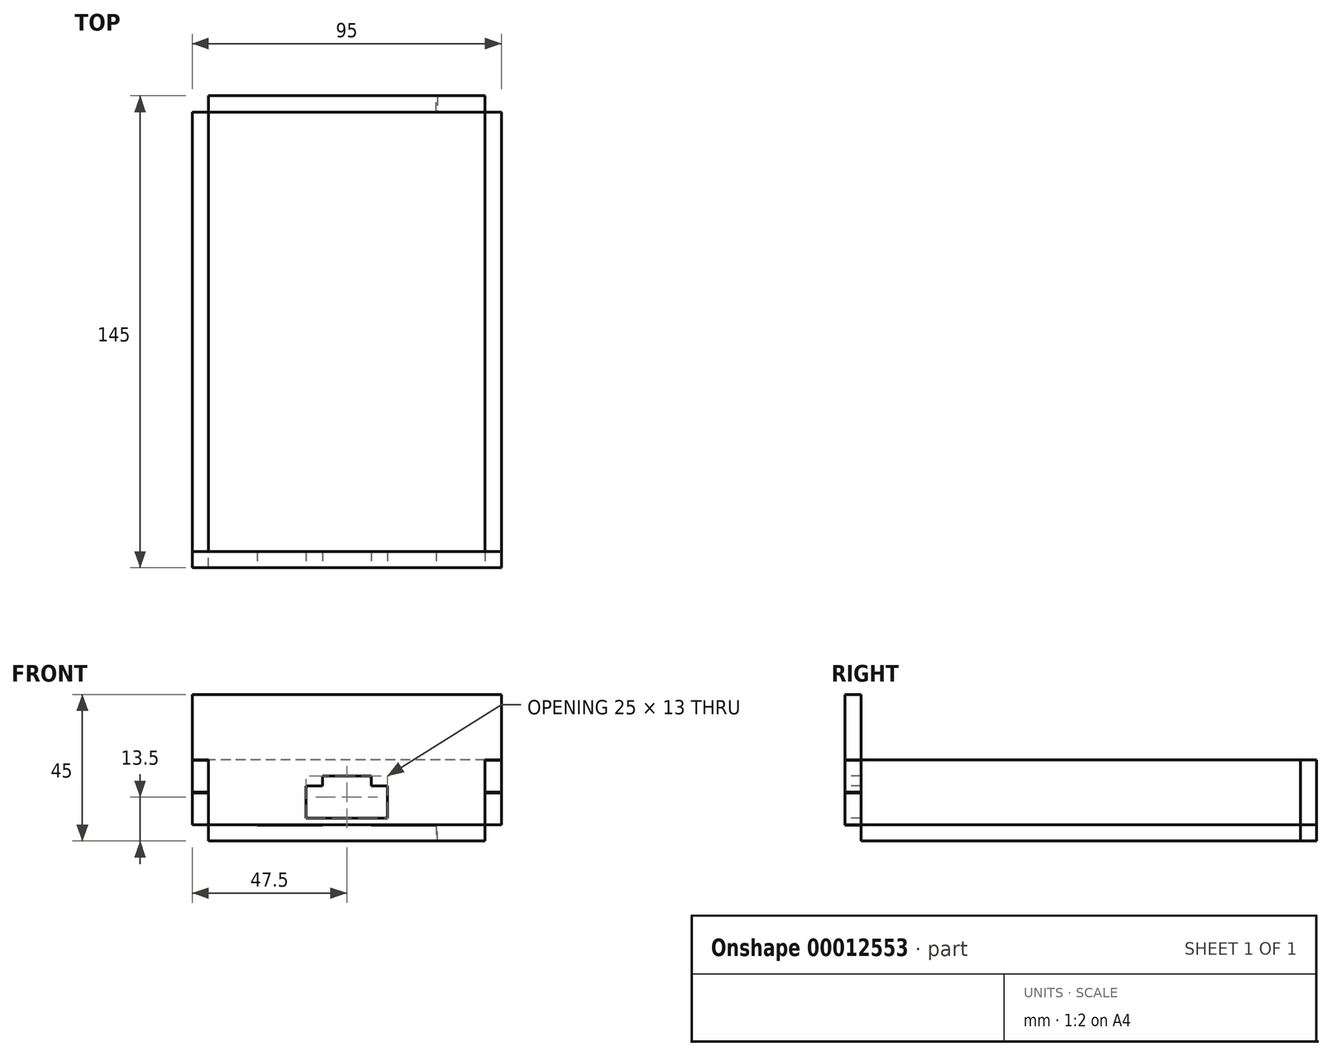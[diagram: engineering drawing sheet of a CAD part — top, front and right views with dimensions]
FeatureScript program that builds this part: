
annotation { "Feature Type Name" : "Feature", "Feature Type Description" : "" }
export const myFeature = defineFeature(function(context is Context, id is Id, definition is map)
    precondition{}
    {
        {
            var Q0;
            Q0=qCreatedBy(makeId("Top.planeOp"),FACE);
            var sketch = newSketch(context, id + "F0", { "sketchPlane" : qUnion([Q0])});
            skLineSegment(sketch, "E0.bottom", {"start": v(0, 0) * mm, "end": v(-95, 0) * mm});
            skLineSegment(sketch, "E0.top", {"start": v(0, 145) * mm, "end": v(-95, 145) * mm});
            skLineSegment(sketch, "E0.left", {"start": v(0, 0) * mm, "end": v(0, 145) * mm});
            skLineSegment(sketch, "E0.right", {"start": v(-95, 0) * mm, "end": v(-95, 145) * mm});
            skSolve(sketch);
        }
        {
            var Q0;
            Q0 = qSketchRegion(id + "F0", true);
            extrude(context, id + "F1", {"entities" : qUnion([Q0]), "depth" : 5 * mm});
        }
        {
            var Q0;
            Q0=makeQuery(id+"F1.opExtrude","SWEPT_FACE",FACE,{"disambiguationData":[OSD([sQuery(id+"F0.wireOp",EDGE,"E0.bottom")])]});
            var sketch = newSketch(context, id + "F2", { "sketchPlane" : qUnion([Q0])});
            skLineSegment(sketch, "E1.bottom", {"start": v(0, 0) * mm, "end": v(-95, 0) * mm});
            skLineSegment(sketch, "E1.top", {"start": v(0, 45) * mm, "end": v(-95, 45) * mm});
            skLineSegment(sketch, "E1.left", {"start": v(0, 0) * mm, "end": v(0, 45) * mm});
            skLineSegment(sketch, "E1.right", {"start": v(-95, 0) * mm, "end": v(-95, 45) * mm});
            skSolve(sketch);
        }
        {
            var Q0;
            Q0 = qSketchRegion(id + "F2", true);
            extrude(context, id + "F3", {"entities" : qUnion([Q0]), "oppositeDirection" : true, "depth" : 5 * mm});
        }
        {
            var Q0;
            Q0=makeQuery(id+"F1.opExtrude","SWEPT_FACE",FACE,{"disambiguationData":[OSD([sQuery(id+"F0.wireOp",EDGE,"E0.left")])]});
            var sketch = newSketch(context, id + "F4", { "sketchPlane" : qUnion([Q0])});
            skLineSegment(sketch, "E2.bottom", {"start": v(0, 0) * mm, "end": v(145, 0) * mm});
            skLineSegment(sketch, "E2.top", {"start": v(0, 25) * mm, "end": v(145, 25) * mm});
            skLineSegment(sketch, "E2.left", {"start": v(0, 0) * mm, "end": v(0, 25) * mm});
            skLineSegment(sketch, "E2.right", {"start": v(145, 0) * mm, "end": v(145, 25) * mm});
            skSolve(sketch);
        }
        {
            var Q0;
            Q0 = qSketchRegion(id + "F4", true);
            extrude(context, id + "F5", {"entities" : qUnion([Q0]), "oppositeDirection" : true, "depth" : 5 * mm});
        }
        {
            var Q0;
            Q0=makeQuery(id+"F1.opExtrude","SWEPT_FACE",FACE,{"disambiguationData":[OSD([sQuery(id+"F0.wireOp",EDGE,"E0.right")])]});
            var sketch = newSketch(context, id + "F6", { "sketchPlane" : qUnion([Q0])});
            skLineSegment(sketch, "E3.bottom", {"start": v(-145, 0) * mm, "end": v(0, 0) * mm});
            skLineSegment(sketch, "E3.top", {"start": v(-145, 25) * mm, "end": v(0, 25) * mm});
            skLineSegment(sketch, "E3.left", {"start": v(-145, 0) * mm, "end": v(-145, 25) * mm});
            skLineSegment(sketch, "E3.right", {"start": v(0, 0) * mm, "end": v(0, 25) * mm});
            skSolve(sketch);
        }
        {
            var Q0;
            Q0 = qSketchRegion(id + "F6", true);
            extrude(context, id + "F7", {"entities" : qUnion([Q0]), "oppositeDirection" : true, "depth" : 5 * mm});
        }
        {
            var Q0;
            Q0=makeQuery(id+"F1.opExtrude","SWEPT_FACE",FACE,{"disambiguationData":[OSD([sQuery(id+"F0.wireOp",EDGE,"E0.top")])]});
            var sketch = newSketch(context, id + "F8", { "sketchPlane" : qUnion([Q0])});
            skLineSegment(sketch, "E4.bottom", {"start": v(0, 0) * mm, "end": v(95, 0) * mm});
            skLineSegment(sketch, "E4.top", {"start": v(0, 25) * mm, "end": v(95, 25) * mm});
            skLineSegment(sketch, "E4.left", {"start": v(0, 0) * mm, "end": v(0, 25) * mm});
            skLineSegment(sketch, "E4.right", {"start": v(95, 0) * mm, "end": v(95, 25) * mm});
            skSolve(sketch);
        }
        {
            var Q0;
            Q0 = qSketchRegion(id + "F8", true);
            extrude(context, id + "F9", {"entities" : qUnion([Q0]), "oppositeDirection" : true, "depth" : 5 * mm});
        }
        {
            var Q0;
            Q0=makeQuery(id+"F7.opExtrude","CAP_FACE",FACE,{"disambiguationData":[OSD([sQuery(id+"F6.wireOp",EDGE,"E3.bottom"),sQuery(id+"F6.wireOp",EDGE,"E3.top"),sQuery(id+"F6.wireOp",EDGE,"E3.left"),sQuery(id+"F6.wireOp",EDGE,"E3.right")])],"isStart":true});
            var sketch = newSketch(context, id + "F10", { "sketchPlane" : qUnion([Q0])});
            skLineSegment(sketch, "E5.bottom", {"start": v(0, 20) * mm, "end": v(-5, 20) * mm});
            skLineSegment(sketch, "E5.top", {"start": v(0, 15) * mm, "end": v(-5, 15) * mm});
            skLineSegment(sketch, "E5.left", {"start": v(0, 20) * mm, "end": v(0, 15) * mm});
            skLineSegment(sketch, "E5.right", {"start": v(-5, 20) * mm, "end": v(-5, 15) * mm});
            skLineSegment(sketch, "E6.bottom", {"start": v(0, 10) * mm, "end": v(-5, 10) * mm});
            skLineSegment(sketch, "E6.top", {"start": v(0, 5) * mm, "end": v(-5, 5) * mm});
            skLineSegment(sketch, "E6.left", {"start": v(0, 10) * mm, "end": v(0, 5) * mm});
            skLineSegment(sketch, "E6.right", {"start": v(-5, 10) * mm, "end": v(-5, 5) * mm});
            skLineSegment(sketch, "E7.bottom", {"start": v(-145, 20) * mm, "end": v(-140, 20) * mm});
            skLineSegment(sketch, "E7.top", {"start": v(-145, 15) * mm, "end": v(-140, 15) * mm});
            skLineSegment(sketch, "E7.left", {"start": v(-145, 20) * mm, "end": v(-145, 15) * mm});
            skLineSegment(sketch, "E7.right", {"start": v(-140, 20) * mm, "end": v(-140, 15) * mm});
            skLineSegment(sketch, "E8.bottom", {"start": v(-145, 10) * mm, "end": v(-140, 10) * mm});
            skLineSegment(sketch, "E8.top", {"start": v(-145, 5) * mm, "end": v(-140, 5) * mm});
            skLineSegment(sketch, "E8.left", {"start": v(-145, 10) * mm, "end": v(-145, 5) * mm});
            skLineSegment(sketch, "E8.right", {"start": v(-140, 10) * mm, "end": v(-140, 5) * mm});
            skLineSegment(sketch, "E9.bottom", {"start": v(-115, 0) * mm, "end": v(-85, 0) * mm});
            skLineSegment(sketch, "E9.top", {"start": v(-115, 5) * mm, "end": v(-85, 5) * mm});
            skLineSegment(sketch, "E9.left", {"start": v(-115, 0) * mm, "end": v(-115, 5) * mm});
            skLineSegment(sketch, "E9.right", {"start": v(-85, 0) * mm, "end": v(-85, 5) * mm});
            skLineSegment(sketch, "E10.bottom", {"start": v(-60, 0) * mm, "end": v(-30, 0) * mm});
            skLineSegment(sketch, "E10.top", {"start": v(-60, 5) * mm, "end": v(-30, 5) * mm});
            skLineSegment(sketch, "E10.left", {"start": v(-60, 0) * mm, "end": v(-60, 5) * mm});
            skLineSegment(sketch, "E10.right", {"start": v(-30, 0) * mm, "end": v(-30, 5) * mm});
            skSolve(sketch);
        }
        {
            var Q0;
            Q0 = qSketchRegion(id + "F10", true);
            extrude(context, id + "F11", {"entities" : qUnion([Q0]), "operationType" : NewBodyOperationType.REMOVE, "oppositeDirection" : true, "depth" : 5 * mm});
        }
        {
            var Q0;
            Q0=makeQuery(id+"F5.opExtrude","CAP_FACE",FACE,{"disambiguationData":[OSD([sQuery(id+"F4.wireOp",EDGE,"E2.bottom"),sQuery(id+"F4.wireOp",EDGE,"E2.top"),sQuery(id+"F4.wireOp",EDGE,"E2.left"),sQuery(id+"F4.wireOp",EDGE,"E2.right")])],"isStart":true});
            var sketch = newSketch(context, id + "F12", { "sketchPlane" : qUnion([Q0])});
            skLineSegment(sketch, "E11.bottom", {"start": v(0, 20) * mm, "end": v(5, 20) * mm});
            skLineSegment(sketch, "E11.top", {"start": v(0, 15) * mm, "end": v(5, 15) * mm});
            skLineSegment(sketch, "E11.left", {"start": v(0, 20) * mm, "end": v(0, 15) * mm});
            skLineSegment(sketch, "E11.right", {"start": v(5, 20) * mm, "end": v(5, 15) * mm});
            skLineSegment(sketch, "E12.bottom", {"start": v(0, 10) * mm, "end": v(5, 10) * mm});
            skLineSegment(sketch, "E12.top", {"start": v(0, 5) * mm, "end": v(5, 5) * mm});
            skLineSegment(sketch, "E12.left", {"start": v(0, 10) * mm, "end": v(0, 5) * mm});
            skLineSegment(sketch, "E12.right", {"start": v(5, 10) * mm, "end": v(5, 5) * mm});
            skLineSegment(sketch, "E13.bottom", {"start": v(30, 0) * mm, "end": v(60, 0) * mm});
            skLineSegment(sketch, "E13.top", {"start": v(30, 5) * mm, "end": v(60, 5) * mm});
            skLineSegment(sketch, "E13.left", {"start": v(30, 0) * mm, "end": v(30, 5) * mm});
            skLineSegment(sketch, "E13.right", {"start": v(60, 0) * mm, "end": v(60, 5) * mm});
            skLineSegment(sketch, "E14.bottom", {"start": v(85, 0) * mm, "end": v(115, 0) * mm});
            skLineSegment(sketch, "E14.top", {"start": v(85, 5) * mm, "end": v(115, 5) * mm});
            skLineSegment(sketch, "E14.left", {"start": v(85, 0) * mm, "end": v(85, 5) * mm});
            skLineSegment(sketch, "E14.right", {"start": v(115, 0) * mm, "end": v(115, 5) * mm});
            skLineSegment(sketch, "E15.bottom", {"start": v(145, 20) * mm, "end": v(140, 20) * mm});
            skLineSegment(sketch, "E15.top", {"start": v(145, 15) * mm, "end": v(140, 15) * mm});
            skLineSegment(sketch, "E15.left", {"start": v(145, 20) * mm, "end": v(145, 15) * mm});
            skLineSegment(sketch, "E15.right", {"start": v(140, 20) * mm, "end": v(140, 15) * mm});
            skLineSegment(sketch, "E16.bottom", {"start": v(145, 10) * mm, "end": v(140, 10) * mm});
            skLineSegment(sketch, "E16.top", {"start": v(145, 5) * mm, "end": v(140, 5) * mm});
            skLineSegment(sketch, "E16.left", {"start": v(145, 10) * mm, "end": v(145, 5) * mm});
            skLineSegment(sketch, "E16.right", {"start": v(140, 10) * mm, "end": v(140, 5) * mm});
            skSolve(sketch);
        }
        {
            var Q0;
            Q0 = qSketchRegion(id + "F12", true);
            extrude(context, id + "F13", {"entities" : qUnion([Q0]), "operationType" : NewBodyOperationType.REMOVE, "oppositeDirection" : true, "depth" : 5 * mm});
        }
        {
            var Q0;
            Q0=makeQuery(id+"F9.opExtrude","CAP_FACE",FACE,{"disambiguationData":[OSD([sQuery(id+"F8.wireOp",EDGE,"E4.bottom"),sQuery(id+"F8.wireOp",EDGE,"E4.top"),sQuery(id+"F8.wireOp",EDGE,"E4.left"),sQuery(id+"F8.wireOp",EDGE,"E4.right")])],"isStart":true});
            var sketch = newSketch(context, id + "F14", { "sketchPlane" : qUnion([Q0])});
            skLineSegment(sketch, "E17.bottom", {"start": v(0, 20) * mm, "end": v(5, 20) * mm});
            skLineSegment(sketch, "E17.top", {"start": v(0, 25) * mm, "end": v(5, 25) * mm});
            skLineSegment(sketch, "E17.left", {"start": v(0, 20) * mm, "end": v(0, 25) * mm});
            skLineSegment(sketch, "E17.right", {"start": v(5, 20) * mm, "end": v(5, 25) * mm});
            skLineSegment(sketch, "E18.bottom", {"start": v(5, 15) * mm, "end": v(0, 15) * mm});
            skLineSegment(sketch, "E18.top", {"start": v(5, 10) * mm, "end": v(0, 10) * mm});
            skLineSegment(sketch, "E18.left", {"start": v(5, 15) * mm, "end": v(5, 10) * mm});
            skLineSegment(sketch, "E18.right", {"start": v(0, 15) * mm, "end": v(0, 10) * mm});
            skLineSegment(sketch, "E19.bottom", {"start": v(5, 5) * mm, "end": v(0, 5) * mm});
            skLineSegment(sketch, "E19.top", {"start": v(5, 0) * mm, "end": v(0, 0) * mm});
            skLineSegment(sketch, "E19.left", {"start": v(5, 5) * mm, "end": v(5, 0) * mm});
            skLineSegment(sketch, "E19.right", {"start": v(0, 5) * mm, "end": v(0, 0) * mm});
            skLineSegment(sketch, "E20.bottom", {"start": v(95, 25) * mm, "end": v(90, 25) * mm});
            skLineSegment(sketch, "E20.top", {"start": v(95, 20) * mm, "end": v(90, 20) * mm});
            skLineSegment(sketch, "E20.left", {"start": v(95, 25) * mm, "end": v(95, 20) * mm});
            skLineSegment(sketch, "E20.right", {"start": v(90, 25) * mm, "end": v(90, 20) * mm});
            skLineSegment(sketch, "E21.bottom", {"start": v(95, 15) * mm, "end": v(90, 15) * mm});
            skLineSegment(sketch, "E21.top", {"start": v(95, 10) * mm, "end": v(90, 10) * mm});
            skLineSegment(sketch, "E21.left", {"start": v(95, 15) * mm, "end": v(95, 10) * mm});
            skLineSegment(sketch, "E21.right", {"start": v(90, 15) * mm, "end": v(90, 10) * mm});
            skLineSegment(sketch, "E22.bottom", {"start": v(95, 5) * mm, "end": v(90, 5) * mm});
            skLineSegment(sketch, "E22.top", {"start": v(95, 0) * mm, "end": v(90, 0) * mm});
            skLineSegment(sketch, "E22.left", {"start": v(95, 5) * mm, "end": v(95, 0) * mm});
            skLineSegment(sketch, "E22.right", {"start": v(90, 5) * mm, "end": v(90, 0) * mm});
            skLineSegment(sketch, "E23.bottom", {"start": v(20, 5) * mm, "end": v(40, 5) * mm});
            skLineSegment(sketch, "E23.top", {"start": v(20, 0) * mm, "end": v(40, 0) * mm});
            skLineSegment(sketch, "E23.left", {"start": v(20, 5) * mm, "end": v(20, 0) * mm});
            skLineSegment(sketch, "E23.right", {"start": v(40, 5) * mm, "end": v(40, 0) * mm});
            skLineSegment(sketch, "E24.bottom", {"start": v(55, 5) * mm, "end": v(75, 5) * mm});
            skLineSegment(sketch, "E24.top", {"start": v(55, 0) * mm, "end": v(75, 0) * mm});
            skLineSegment(sketch, "E24.left", {"start": v(55, 5) * mm, "end": v(55, 0) * mm});
            skLineSegment(sketch, "E24.right", {"start": v(75, 5) * mm, "end": v(75, 0) * mm});
            skSolve(sketch);
        }
        {
            var Q0;
            Q0 = qSketchRegion(id + "F14", true);
            extrude(context, id + "F15", {"entities" : qUnion([Q0]), "operationType" : NewBodyOperationType.REMOVE, "oppositeDirection" : true, "depth" : 5 * mm});
        }
        {
            var Q0;
            Q0=makeQuery(id+"F3.opExtrude","CAP_FACE",FACE,{"disambiguationData":[OSD([sQuery(id+"F2.wireOp",EDGE,"E1.bottom"),sQuery(id+"F2.wireOp",EDGE,"E1.top"),sQuery(id+"F2.wireOp",EDGE,"E1.left"),sQuery(id+"F2.wireOp",EDGE,"E1.right")])],"isStart":true});
            var sketch = newSketch(context, id + "F16", { "sketchPlane" : qUnion([Q0])});
            skLineSegment(sketch, "E25.bottom", {"start": v(-95, 24.84) * mm, "end": v(-90, 24.84) * mm});
            skLineSegment(sketch, "E25.top", {"start": v(-95, 19.84) * mm, "end": v(-90, 19.84) * mm});
            skLineSegment(sketch, "E25.left", {"start": v(-95, 24.84) * mm, "end": v(-95, 19.84) * mm});
            skLineSegment(sketch, "E25.right", {"start": v(-90, 24.84) * mm, "end": v(-90, 19.84) * mm});
            skLineSegment(sketch, "E26.bottom", {"start": v(-95, 14.84) * mm, "end": v(-90, 14.84) * mm});
            skLineSegment(sketch, "E26.top", {"start": v(-95, 9.84) * mm, "end": v(-90, 9.84) * mm});
            skLineSegment(sketch, "E26.left", {"start": v(-95, 14.84) * mm, "end": v(-95, 9.84) * mm});
            skLineSegment(sketch, "E26.right", {"start": v(-90, 14.84) * mm, "end": v(-90, 9.84) * mm});
            skLineSegment(sketch, "E27.bottom", {"start": v(-95, 4.84) * mm, "end": v(-90, 4.84) * mm});
            skLineSegment(sketch, "E27.top", {"start": v(-95, 0) * mm, "end": v(-90, 0) * mm});
            skLineSegment(sketch, "E27.left", {"start": v(-95, 4.84) * mm, "end": v(-95, 0) * mm});
            skLineSegment(sketch, "E27.right", {"start": v(-90, 4.84) * mm, "end": v(-90, 0) * mm});
            skLineSegment(sketch, "E28.bottom", {"start": v(0, 24.84) * mm, "end": v(-5, 24.84) * mm});
            skLineSegment(sketch, "E28.top", {"start": v(0, 19.84) * mm, "end": v(-5, 19.84) * mm});
            skLineSegment(sketch, "E28.left", {"start": v(0, 24.84) * mm, "end": v(0, 19.84) * mm});
            skLineSegment(sketch, "E28.right", {"start": v(-5, 24.84) * mm, "end": v(-5, 19.84) * mm});
            skLineSegment(sketch, "E29.bottom", {"start": v(0, 14.84) * mm, "end": v(-5, 14.84) * mm});
            skLineSegment(sketch, "E29.top", {"start": v(0, 9.84) * mm, "end": v(-5, 9.84) * mm});
            skLineSegment(sketch, "E29.left", {"start": v(0, 14.84) * mm, "end": v(0, 9.84) * mm});
            skLineSegment(sketch, "E29.right", {"start": v(-5, 14.84) * mm, "end": v(-5, 9.84) * mm});
            skLineSegment(sketch, "E30.bottom", {"start": v(0, 4.84) * mm, "end": v(-5, 4.84) * mm});
            skLineSegment(sketch, "E30.top", {"start": v(0, 0) * mm, "end": v(-5, 0) * mm});
            skLineSegment(sketch, "E30.left", {"start": v(0, 4.84) * mm, "end": v(0, 0) * mm});
            skLineSegment(sketch, "E30.right", {"start": v(-5, 4.84) * mm, "end": v(-5, 0) * mm});
            skLineSegment(sketch, "E31.bottom", {"start": v(-75, 0) * mm, "end": v(-55, 0) * mm});
            skLineSegment(sketch, "E31.top", {"start": v(-75, 4.84) * mm, "end": v(-55, 4.84) * mm});
            skLineSegment(sketch, "E31.left", {"start": v(-75, 0) * mm, "end": v(-75, 4.84) * mm});
            skLineSegment(sketch, "E31.right", {"start": v(-55, 0) * mm, "end": v(-55, 4.84) * mm});
            skLineSegment(sketch, "E32.bottom", {"start": v(-40, 0) * mm, "end": v(-20, 0) * mm});
            skLineSegment(sketch, "E32.top", {"start": v(-40, 4.84) * mm, "end": v(-20, 4.84) * mm});
            skLineSegment(sketch, "E32.left", {"start": v(-40, 0) * mm, "end": v(-40, 4.84) * mm});
            skLineSegment(sketch, "E32.right", {"start": v(-20, 0) * mm, "end": v(-20, 4.84) * mm});
            skLineSegment(sketch, "E33.bottom", {"start": v(-60, 17) * mm, "end": v(-35, 17) * mm});
            skLineSegment(sketch, "E33.top", {"start": v(-60, 7) * mm, "end": v(-35, 7) * mm});
            skLineSegment(sketch, "E33.left", {"start": v(-60, 17) * mm, "end": v(-60, 7) * mm});
            skLineSegment(sketch, "E33.right", {"start": v(-35, 17) * mm, "end": v(-35, 7) * mm});
            skLineSegment(sketch, "E34.bottom", {"start": v(-55, 17) * mm, "end": v(-40, 17) * mm});
            skLineSegment(sketch, "E34.top", {"start": v(-55, 20) * mm, "end": v(-40, 20) * mm});
            skLineSegment(sketch, "E34.left", {"start": v(-55, 17) * mm, "end": v(-55, 20) * mm});
            skLineSegment(sketch, "E34.right", {"start": v(-40, 17) * mm, "end": v(-40, 20) * mm});
            skSolve(sketch);
        }
        {
            var Q0;
            Q0 = qSketchRegion(id + "F16", true);
            extrude(context, id + "F17", {"entities" : qUnion([Q0]), "operationType" : NewBodyOperationType.REMOVE, "oppositeDirection" : true, "depth" : 5 * mm});
        }
        {
            var Q0;
            Q0=makeQuery(id+"F1.opExtrude","CAP_FACE",FACE,{"disambiguationData":[OSD([sQuery(id+"F0.wireOp",EDGE,"E0.bottom"),sQuery(id+"F0.wireOp",EDGE,"E0.top"),sQuery(id+"F0.wireOp",EDGE,"E0.left"),sQuery(id+"F0.wireOp",EDGE,"E0.right")])],"isStart":false});
            var sketch = newSketch(context, id + "F18", { "sketchPlane" : qUnion([Q0])});
            skLineSegment(sketch, "E35.bottom", {"start": v(0, 0) * mm, "end": v(-20, 0) * mm});
            skLineSegment(sketch, "E35.top", {"start": v(0, 5) * mm, "end": v(-20, 5) * mm});
            skLineSegment(sketch, "E35.left", {"start": v(0, 0) * mm, "end": v(0, 5) * mm});
            skLineSegment(sketch, "E35.right", {"start": v(-20, 0) * mm, "end": v(-20, 5) * mm});
            skLineSegment(sketch, "E36.bottom", {"start": v(-40, 0) * mm, "end": v(-55, 0) * mm});
            skLineSegment(sketch, "E36.top", {"start": v(-40, 5) * mm, "end": v(-55, 5) * mm});
            skLineSegment(sketch, "E36.left", {"start": v(-40, 0) * mm, "end": v(-40, 5) * mm});
            skLineSegment(sketch, "E36.right", {"start": v(-55, 0) * mm, "end": v(-55, 5) * mm});
            skLineSegment(sketch, "E37.bottom", {"start": v(-75, 0) * mm, "end": v(-95, 0) * mm});
            skLineSegment(sketch, "E37.top", {"start": v(-75, 5) * mm, "end": v(-95, 5) * mm});
            skLineSegment(sketch, "E37.left", {"start": v(-75, 0) * mm, "end": v(-75, 5) * mm});
            skLineSegment(sketch, "E37.right", {"start": v(-95, 0) * mm, "end": v(-95, 5) * mm});
            skLineSegment(sketch, "E38.bottom", {"start": v(0, 0) * mm, "end": v(-5, 0) * mm});
            skLineSegment(sketch, "E38.top", {"start": v(0, 30) * mm, "end": v(-5, 30) * mm});
            skLineSegment(sketch, "E38.left", {"start": v(0, 0) * mm, "end": v(0, 30) * mm});
            skLineSegment(sketch, "E38.right", {"start": v(-5, 0) * mm, "end": v(-5, 30) * mm});
            skLineSegment(sketch, "E39.bottom", {"start": v(0, 60) * mm, "end": v(-5, 60) * mm});
            skLineSegment(sketch, "E39.top", {"start": v(0, 85) * mm, "end": v(-5, 85) * mm});
            skLineSegment(sketch, "E39.left", {"start": v(0, 60) * mm, "end": v(0, 85) * mm});
            skLineSegment(sketch, "E39.right", {"start": v(-5, 60) * mm, "end": v(-5, 85) * mm});
            skLineSegment(sketch, "E40.bottom", {"start": v(0, 115) * mm, "end": v(-5, 115) * mm});
            skLineSegment(sketch, "E40.top", {"start": v(0, 145) * mm, "end": v(-5, 145) * mm});
            skLineSegment(sketch, "E40.left", {"start": v(0, 115) * mm, "end": v(0, 145) * mm});
            skLineSegment(sketch, "E40.right", {"start": v(-5, 115) * mm, "end": v(-5, 145) * mm});
            skLineSegment(sketch, "E41.bottom", {"start": v(0, 145) * mm, "end": v(-19.7, 145) * mm});
            skLineSegment(sketch, "E41.top", {"start": v(0, 140) * mm, "end": v(-19.7, 140) * mm});
            skLineSegment(sketch, "E41.left", {"start": v(0, 145) * mm, "end": v(0, 140) * mm});
            skLineSegment(sketch, "E41.right", {"start": v(-19.7, 145) * mm, "end": v(-19.7, 140) * mm});
            skLineSegment(sketch, "E42.bottom", {"start": v(-39.7, 145) * mm, "end": v(-55, 145) * mm});
            skLineSegment(sketch, "E42.top", {"start": v(-39.7, 140) * mm, "end": v(-55, 140) * mm});
            skLineSegment(sketch, "E42.left", {"start": v(-39.7, 145) * mm, "end": v(-39.7, 140) * mm});
            skLineSegment(sketch, "E42.right", {"start": v(-55, 145) * mm, "end": v(-55, 140) * mm});
            skLineSegment(sketch, "E43.bottom", {"start": v(-75, 145) * mm, "end": v(-95, 145) * mm});
            skLineSegment(sketch, "E43.top", {"start": v(-75, 140) * mm, "end": v(-95, 140) * mm});
            skLineSegment(sketch, "E43.left", {"start": v(-75, 145) * mm, "end": v(-75, 140) * mm});
            skLineSegment(sketch, "E43.right", {"start": v(-95, 145) * mm, "end": v(-95, 140) * mm});
            skLineSegment(sketch, "E44.bottom", {"start": v(-95, 145) * mm, "end": v(-90, 145) * mm});
            skLineSegment(sketch, "E44.top", {"start": v(-95, 115) * mm, "end": v(-90, 115) * mm});
            skLineSegment(sketch, "E44.left", {"start": v(-95, 145) * mm, "end": v(-95, 115) * mm});
            skLineSegment(sketch, "E44.right", {"start": v(-90, 145) * mm, "end": v(-90, 115) * mm});
            skLineSegment(sketch, "E45.bottom", {"start": v(-95, 85) * mm, "end": v(-90, 85) * mm});
            skLineSegment(sketch, "E45.top", {"start": v(-95, 60) * mm, "end": v(-90, 60) * mm});
            skLineSegment(sketch, "E45.left", {"start": v(-95, 85) * mm, "end": v(-95, 60) * mm});
            skLineSegment(sketch, "E45.right", {"start": v(-90, 85) * mm, "end": v(-90, 60) * mm});
            skLineSegment(sketch, "E46.bottom", {"start": v(-95, 30) * mm, "end": v(-90, 30) * mm});
            skLineSegment(sketch, "E46.top", {"start": v(-95, 0) * mm, "end": v(-90, 0) * mm});
            skLineSegment(sketch, "E46.left", {"start": v(-95, 30) * mm, "end": v(-95, 0) * mm});
            skLineSegment(sketch, "E46.right", {"start": v(-90, 30) * mm, "end": v(-90, 0) * mm});
            skSolve(sketch);
        }
        {
            var Q0;
            Q0 = qSketchRegion(id + "F18", true);
            extrude(context, id + "F19", {"entities" : qUnion([Q0]), "operationType" : NewBodyOperationType.REMOVE, "oppositeDirection" : true, "depth" : 5 * mm});
        }
        {
            var Q0;
            Q0=makeQuery(id+"F3.opExtrude","CAP_FACE",FACE,{"disambiguationData":[OSD([sQuery(id+"F2.wireOp",EDGE,"E1.bottom"),sQuery(id+"F2.wireOp",EDGE,"E1.top"),sQuery(id+"F2.wireOp",EDGE,"E1.left"),sQuery(id+"F2.wireOp",EDGE,"E1.right")])],"isStart":true});
            var sketch = newSketch(context, id + "F20", { "sketchPlane" : qUnion([Q0])});
            skLineSegment(sketch, "E47.bottom", {"start": v(-95, 0) * mm, "end": v(0, 0) * mm});
            skLineSegment(sketch, "E47.top", {"start": v(-95, 3) * mm, "end": v(0, 3) * mm});
            skLineSegment(sketch, "E47.left", {"start": v(-95, 0) * mm, "end": v(-95, 3) * mm});
            skLineSegment(sketch, "E47.right", {"start": v(0, 0) * mm, "end": v(0, 3) * mm});
            skSolve(sketch);
        }
        {
            var Q0;
            Q0 = qSketchRegion(id + "F20", true);
            extrude(context, id + "F21", {"entities" : qUnion([Q0]), "operationType" : NewBodyOperationType.REMOVE, "oppositeDirection" : true, "depth" : 5 * mm});
        }
    });
